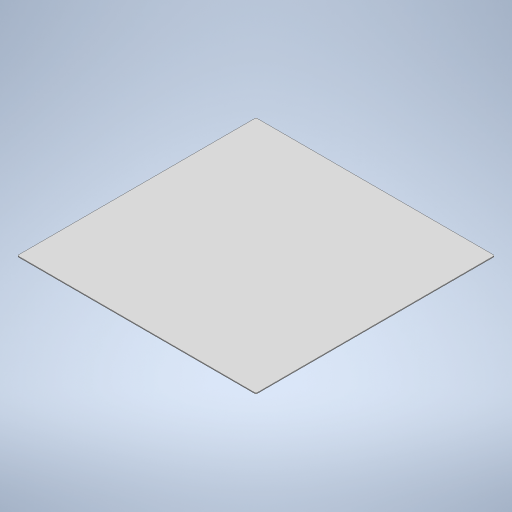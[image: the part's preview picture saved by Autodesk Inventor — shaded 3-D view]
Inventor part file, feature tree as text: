
AUTODESK INVENTOR PART (.ipt)
format: ipt  version: 2023 (Build 270158000, 158)  size: 336,384 bytes
history: native  units: in
note: dims shown in document units (in); Inventor stores cm internally (conversion verified against a paired STEP export)
features: extrude x1, chamfer x1, sketch x1
ambient origin geometry x8: Origin, YZ Plane, XZ Plane, XY Plane, X Axis, Y Axis, Z Axis, Center Point
bodies: Solid1 (feature_tree)
feature tree (3):
  extrude  "Extrusion1"  Depth=54.0in
  chamfer  "Chamfer1"  Distance=1.0in
  sketch  "Sketch1"  dims[d0=54.0in d1=54.0in d2=1.0in d3=1.0in d4=8.0in d5=16.0in d6=8.0in d7=16.0in d8=16.0in d9=8.0in d10=16.0in d11=8.0in d12=4.0in d13=4.0in d14=4.0in d15=4.0in d16=17.0in d17=17.0in d18=17.0in d19=17.0in d20=20.0in d21=1.0in d22=1.0in d23=1.0in d24=1.0in d25=45.0deg d26=2.5in d27=45.0deg d28=45.0deg d29=45.0deg d30=1.0in d31=1.0in d32=1.0in d33=1.0in d34=0.25in d35=0.25in d36=0.25in d37=0.25in d38=0.25in d39=0.25in d40=0.25in d41=0.25in d42=0.2in d43=0.0in d44=0.06in d45=0.125in d46=45.0deg]
